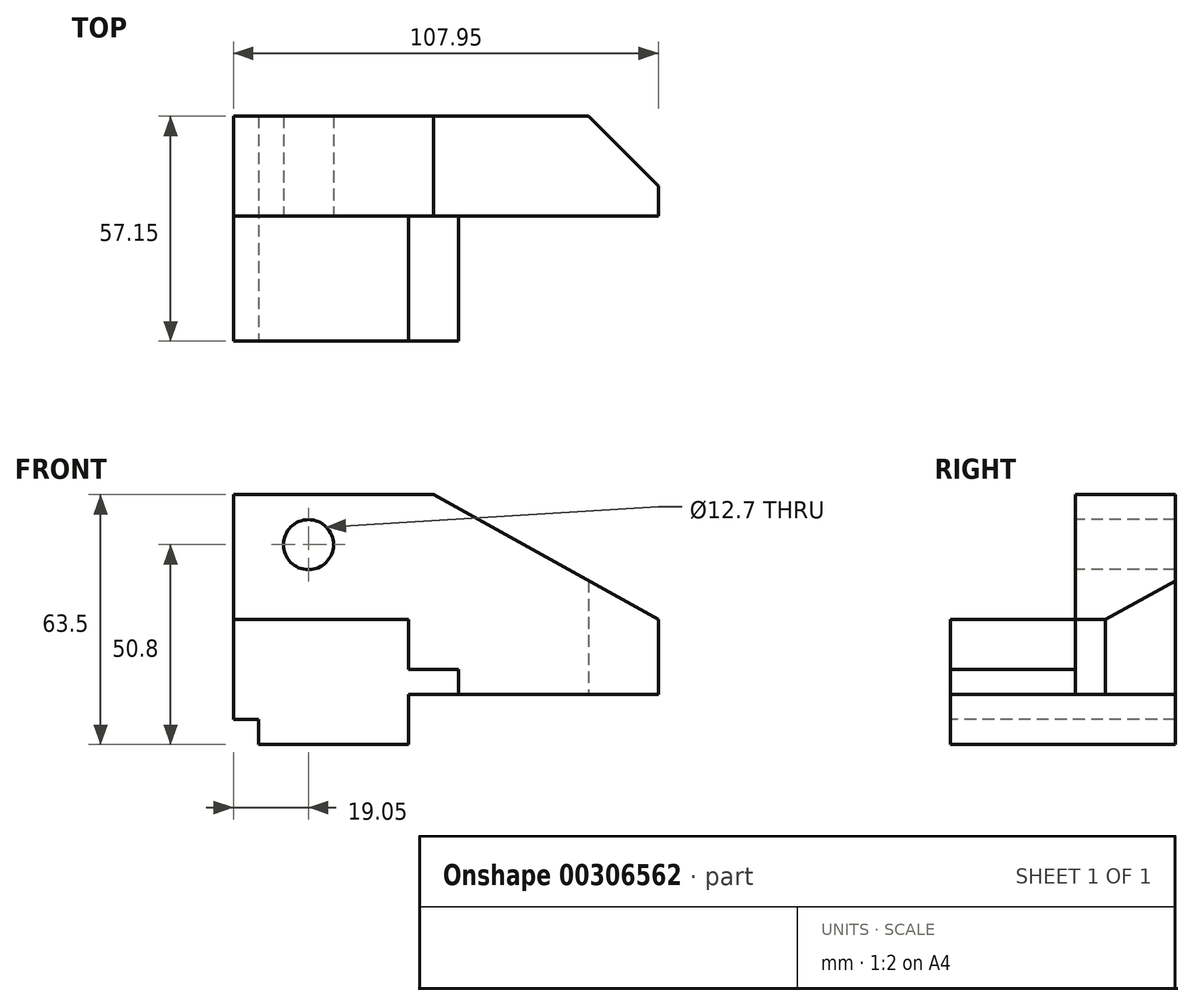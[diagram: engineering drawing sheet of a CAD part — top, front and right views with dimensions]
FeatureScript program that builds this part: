
annotation { "Feature Type Name" : "Feature", "Feature Type Description" : "" }
export const myFeature = defineFeature(function(context is Context, id is Id, definition is map)
    precondition{}
    {
        {
            var Q0;
            Q0=qCreatedBy(makeId("Front.planeOp"),FACE);
            var sketch = newSketch(context, id + "F0", { "sketchPlane" : qUnion([Q0])});
            skLineSegment(sketch, "E0", {"start": v(0, 0) * mm, "end": v(0, 50.8) * mm});
            skLineSegment(sketch, "E1", {"start": v(0, 50.8) * mm, "end": v(50.8, 50.8) * mm});
            skLineSegment(sketch, "E2", {"start": v(0, 0) * mm, "end": v(107.95, 0) * mm});
            skLineSegment(sketch, "E3", {"start": v(107.95, 0) * mm, "end": v(107.95, 19.05) * mm});
            skLineSegment(sketch, "E4", {"start": v(107.95, 19.05) * mm, "end": v(50.8, 50.8) * mm});
            skSolve(sketch);
        }
        {
            var Q0;
            Q0=makeQuery(id+"F0.imprint","IMPRINT",FACE,{"disambiguationData":[TD([[makeQuery(id+"F0.imprint","IMPRINT",EDGE,{"derivedFrom":sQuery(id+"F0.wireOp",EDGE,"E0")}),-1.0]])]});
            extrude(context, id + "F1", {"entities" : qUnion([Q0]), "depth" : 25.4 * mm});
        }
        {
            var Q0;
            Q0=qCreatedBy(makeId("Front.planeOp"),FACE);
            var sketch = newSketch(context, id + "F2", { "sketchPlane" : qUnion([Q0])});
            skLineSegment(sketch, "E5.bottom", {"start": v(0, 19.05) * mm, "end": v(57.15, 19.05) * mm});
            skLineSegment(sketch, "E5.top", {"start": v(0, -12.7) * mm, "end": v(57.15, -12.7) * mm});
            skLineSegment(sketch, "E5.left", {"start": v(0, 19.05) * mm, "end": v(0, -12.7) * mm});
            skLineSegment(sketch, "E5.right", {"start": v(57.15, 19.05) * mm, "end": v(57.15, -12.7) * mm});
            skSolve(sketch);
        }
        {
            var Q0;
            Q0=makeQuery(id+"F2.imprint","IMPRINT",FACE,{"disambiguationData":[TD([[makeQuery(id+"F2.imprint","IMPRINT",EDGE,{"derivedFrom":sQuery(id+"F2.wireOp",EDGE,"E5.bottom")}),-1.0]])]});
            extrude(context, id + "F3", {"entities" : qUnion([Q0]), "operationType" : NewBodyOperationType.ADD, "depth" : 57.15 * mm});
        }
        {
            var Q0;
            Q0=makeQuery(id+"F3.opExtrude","CAP_FACE",FACE,{"disambiguationData":[OSD([sQuery(id+"F2.wireOp",EDGE,"E5.bottom"),sQuery(id+"F2.wireOp",EDGE,"E5.top"),sQuery(id+"F2.wireOp",EDGE,"E5.left"),sQuery(id+"F2.wireOp",EDGE,"E5.right")])],"isStart":false});
            var sketch = newSketch(context, id + "F4", { "sketchPlane" : qUnion([Q0])});
            skLineSegment(sketch, "E6.bottom", {"start": v(0, -6.35) * mm, "end": v(6.35, -6.35) * mm});
            skLineSegment(sketch, "E6.top", {"start": v(0, -12.7) * mm, "end": v(6.35, -12.7) * mm});
            skLineSegment(sketch, "E6.left", {"start": v(0, -6.35) * mm, "end": v(0, -12.7) * mm});
            skLineSegment(sketch, "E6.right", {"start": v(6.35, -6.35) * mm, "end": v(6.35, -12.7) * mm});
            skLineSegment(sketch, "E7.bottom", {"start": v(57.15, 0) * mm, "end": v(44.45, 0) * mm});
            skLineSegment(sketch, "E7.top", {"start": v(57.15, -12.7) * mm, "end": v(44.45, -12.7) * mm});
            skLineSegment(sketch, "E7.left", {"start": v(57.15, 0) * mm, "end": v(57.15, -12.7) * mm});
            skLineSegment(sketch, "E7.right", {"start": v(44.45, 0) * mm, "end": v(44.45, -12.7) * mm});
            skLineSegment(sketch, "E8.bottom", {"start": v(44.45, 19.05) * mm, "end": v(57.15, 19.05) * mm});
            skLineSegment(sketch, "E8.top", {"start": v(44.45, 6.35) * mm, "end": v(57.15, 6.35) * mm});
            skLineSegment(sketch, "E8.left", {"start": v(44.45, 19.05) * mm, "end": v(44.45, 6.35) * mm});
            skLineSegment(sketch, "E8.right", {"start": v(57.15, 19.05) * mm, "end": v(57.15, 6.35) * mm});
            skSolve(sketch);
        }
        {
            var Q0;
            Q0=makeQuery(id+"F4.imprint","IMPRINT",FACE,{"disambiguationData":[TD([[makeQuery(id+"F4.imprint","IMPRINT",EDGE,{"derivedFrom":sQuery(id+"F4.wireOp",EDGE,"E6.bottom")}),-1.0]])]});
            extrude(context, id + "F5", {"entities" : qUnion([Q0]), "operationType" : NewBodyOperationType.REMOVE, "endBound" : BoundingType.THROUGH_ALL, "oppositeDirection" : true, "depth" : 25.4 * mm});
        }
        {
            var Q0;
            Q0=makeQuery(id+"F4.imprint","IMPRINT",FACE,{"disambiguationData":[TD([[makeQuery(id+"F4.imprint","IMPRINT",EDGE,{"derivedFrom":sQuery(id+"F4.wireOp",EDGE,"E8.bottom")}),-1.0]])]});
            var Q1;
            Q1=makeQuery(id+"F4.imprint","IMPRINT",FACE,{"disambiguationData":[TD([[makeQuery(id+"F4.imprint","IMPRINT",EDGE,{"derivedFrom":sQuery(id+"F4.wireOp",EDGE,"E7.bottom")}),1.0]])]});
            extrude(context, id + "F6", {"entities" : qUnion([Q0, Q1]), "operationType" : NewBodyOperationType.REMOVE, "oppositeDirection" : true, "depth" : 31.75 * mm});
        }
        {
            var Q0;
            Q0=makeQuery(id+"F6.boolean.opBoolean","COPY",FACE,{"derivedFrom":makeQuery(id+"F6.opExtrude","CAP_FACE",FACE,{"disambiguationData":[OSD([sQuery(id+"F4.wireOp",EDGE,"E7.bottom"),sQuery(id+"F4.wireOp",EDGE,"E7.top"),sQuery(id+"F4.wireOp",EDGE,"E7.left"),sQuery(id+"F4.wireOp",EDGE,"E7.right")])],"isStart":false})});
            extrude(context, id + "F7", {"entities" : qUnion([Q0]), "operationType" : NewBodyOperationType.REMOVE, "endBound" : BoundingType.THROUGH_ALL, "oppositeDirection" : true, "depth" : 25.4 * mm});
        }
        {
            var Q0;
            Q0=makeQuery(id+"F6.boolean.opBoolean","MERGE",FACE,{"derivedFrom":[makeQuery(id+"F1.opExtrude","CAP_FACE",FACE,{"disambiguationData":[OSD([sQuery(id+"F0.wireOp",EDGE,"E0"),sQuery(id+"F0.wireOp",EDGE,"E1"),sQuery(id+"F0.wireOp",EDGE,"E2"),sQuery(id+"F0.wireOp",EDGE,"E3"),sQuery(id+"F0.wireOp",EDGE,"E4")])],"isStart":false}),makeQuery(id+"F6.opExtrude","CAP_FACE",FACE,{"disambiguationData":[OSD([sQuery(id+"F4.wireOp",EDGE,"E8.bottom"),sQuery(id+"F4.wireOp",EDGE,"E8.top"),sQuery(id+"F4.wireOp",EDGE,"E8.left"),sQuery(id+"F4.wireOp",EDGE,"E8.right")])],"isStart":false})]});
            var sketch = newSketch(context, id + "F8", { "sketchPlane" : qUnion([Q0])});
            skCircle(sketch, "E9", {"center": v(19.05, 38.1) * mm, "radius": 6.35 * mm});
            skSolve(sketch);
        }
        {
            var Q0;
            Q0=makeQuery(id+"F8.imprint","IMPRINT",FACE,{"disambiguationData":[TD([[makeQuery(id+"F8.imprint","IMPRINT",EDGE,{"derivedFrom":sQuery(id+"F8.wireOp",EDGE,"E9")}),1.0]])]});
            extrude(context, id + "F9", {"entities" : qUnion([Q0]), "operationType" : NewBodyOperationType.REMOVE, "endBound" : BoundingType.THROUGH_ALL, "oppositeDirection" : true, "depth" : 25.4 * mm});
        }
        {
            var Q0;
            Q0=makeQuery(id+"F1.opExtrude","CAP_EDGE",EDGE,{"disambiguationData":[OSD([sQuery(id+"F0.wireOp",EDGE,"E3")])],"isStart":true});
            chamfer(context, id + "F10", {"entities" : qUnion([Q0]), "width" : 17.78 * mm, "tangentPropagation" : true});
        }
    });
